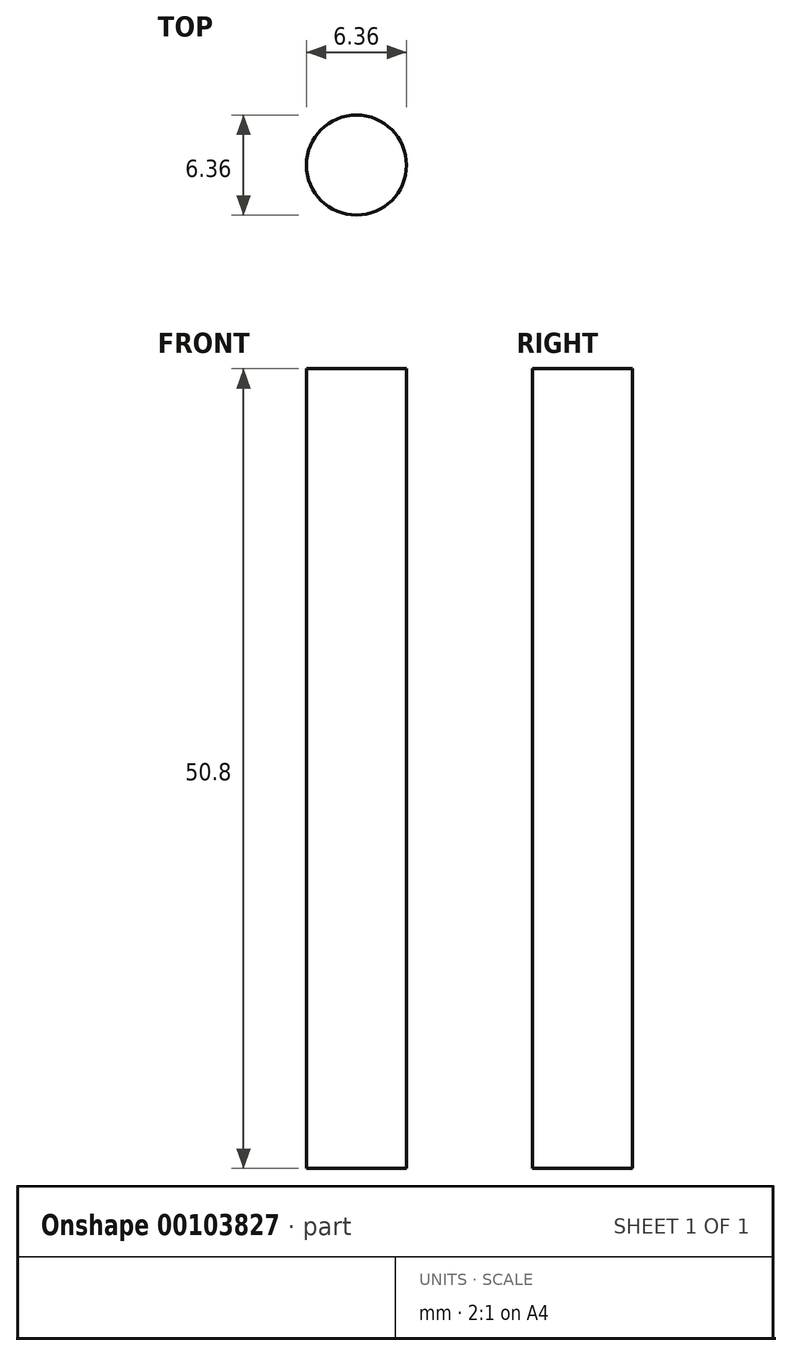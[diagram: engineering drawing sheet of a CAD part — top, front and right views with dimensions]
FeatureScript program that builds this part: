
annotation { "Feature Type Name" : "Feature", "Feature Type Description" : "" }
export const myFeature = defineFeature(function(context is Context, id is Id, definition is map)
    precondition{}
    {
        {
            var Q0;
            Q0=qCreatedBy(makeId("Top.planeOp"),FACE);
            var sketch = newSketch(context, id + "F0", { "sketchPlane" : qUnion([Q0])});
            skCircle(sketch, "E0", {"center": v(0, 0) * mm, "radius": 3.18 * mm});
            skSolve(sketch);
        }
        {
            var Q0;
            Q0 = qSketchRegion(id + "F0", true);
            extrude(context, id + "F1", {"entities" : qUnion([Q0]), "depth" : 50.8 * mm});
        }
    });
